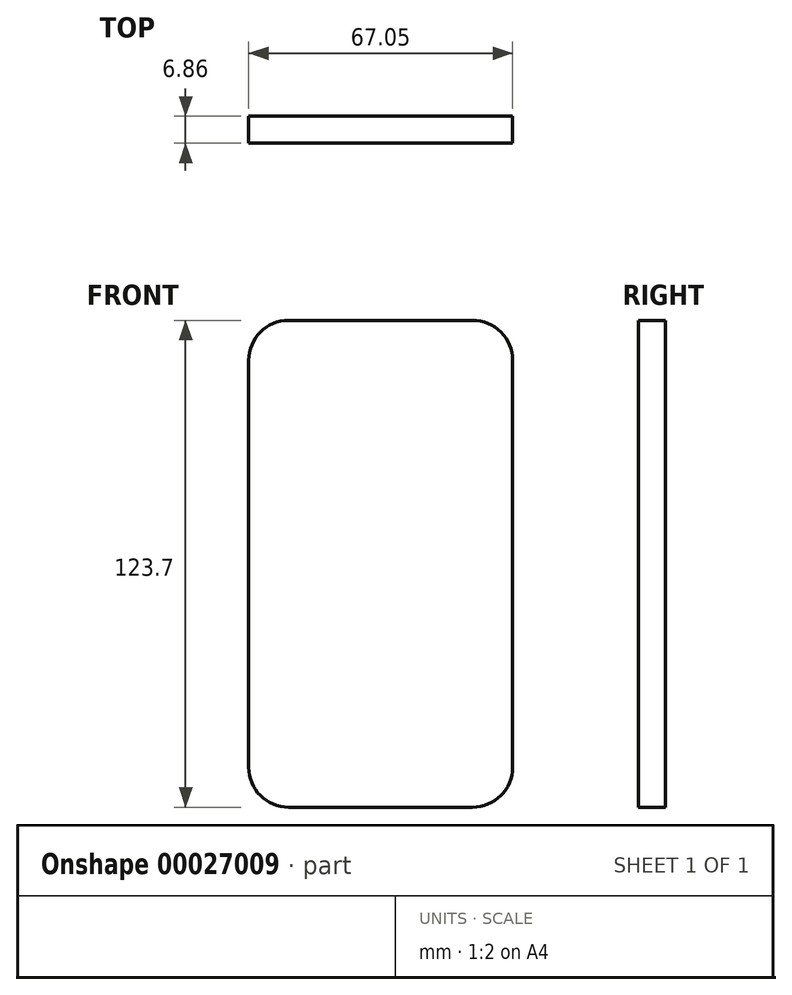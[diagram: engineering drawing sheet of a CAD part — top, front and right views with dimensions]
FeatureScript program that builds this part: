
annotation { "Feature Type Name" : "Feature", "Feature Type Description" : "" }
export const myFeature = defineFeature(function(context is Context, id is Id, definition is map)
    precondition{}
    {
        {
            var Q0;
            Q0=qCreatedBy(makeId("Front.planeOp"),FACE);
            var sketch = newSketch(context, id + "F0", { "sketchPlane" : qUnion([Q0])});
            skLineSegment(sketch, "E0.bottom", {"start": v(25.77, 29.67) * mm, "end": v(-41.28, 29.67) * mm});
            skLineSegment(sketch, "E0.top", {"start": v(25.77, -94.03) * mm, "end": v(-41.28, -94.03) * mm});
            skLineSegment(sketch, "E0.left", {"start": v(25.77, 29.67) * mm, "end": v(25.77, -94.03) * mm});
            skLineSegment(sketch, "E0.right", {"start": v(-41.28, 29.67) * mm, "end": v(-41.28, -94.03) * mm});
            skSolve(sketch);
        }
        {
            var Q0;
            Q0 = qSketchRegion(id + "F0", true);
            extrude(context, id + "F1", {"entities" : qUnion([Q0]), "depth" : 6.86 * mm});
        }
        {
            var Q0;
            Q0=makeQuery(id+"F1.opExtrude","SWEPT_EDGE",EDGE,{"disambiguationData":[OSD([sQuery(id+"F0.wireOp",EDGE,"E0.bottom"),sQuery(id+"F0.wireOp",EDGE,"E0.right")])]});
            var Q1;
            Q1=makeQuery(id+"F1.opExtrude","SWEPT_EDGE",EDGE,{"disambiguationData":[OSD([sQuery(id+"F0.wireOp",EDGE,"E0.bottom"),sQuery(id+"F0.wireOp",EDGE,"E0.left")])]});
            var Q2;
            Q2=makeQuery(id+"F1.opExtrude","SWEPT_EDGE",EDGE,{"disambiguationData":[OSD([sQuery(id+"F0.wireOp",EDGE,"E0.top"),sQuery(id+"F0.wireOp",EDGE,"E0.right")])]});
            var Q3;
            Q3=makeQuery(id+"F1.opExtrude","SWEPT_EDGE",EDGE,{"disambiguationData":[OSD([sQuery(id+"F0.wireOp",EDGE,"E0.top"),sQuery(id+"F0.wireOp",EDGE,"E0.left")])]});
            fillet(context, id + "F2", {"entities" : qUnion([Q0, Q1, Q2, Q3]), "radius" : 10.16 * mm, "tangentPropagation" : true, "allowEdgeOverflow" : false});
        }
    });
